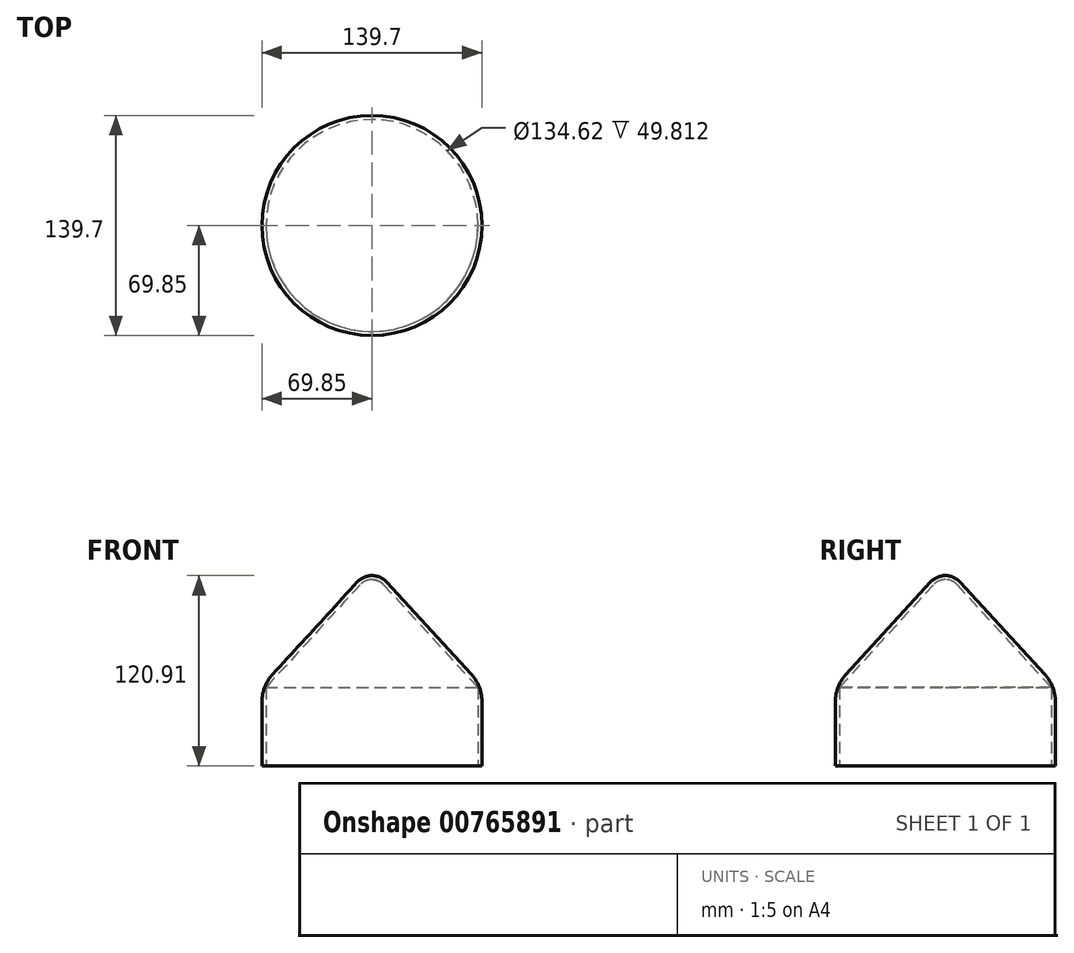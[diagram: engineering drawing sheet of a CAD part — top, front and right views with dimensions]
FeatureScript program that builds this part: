
annotation { "Feature Type Name" : "Feature", "Feature Type Description" : "" }
export const myFeature = defineFeature(function(context is Context, id is Id, definition is map)
    precondition{}
    {
        {
            var Q0;
            Q0=qCreatedBy(makeId("Front.planeOp"),FACE);
            var sketch = newSketch(context, id + "F0", { "sketchPlane" : qUnion([Q0])});
            skLineSegment(sketch, "E0", {"start": v(0, 0) * mm, "end": v(0, 76.2) * mm});
            skLineSegment(sketch, "E1", {"start": v(0, 76.2) * mm, "end": v(69.85, 0) * mm});
            skLineSegment(sketch, "E2", {"start": v(69.85, 0) * mm, "end": v(0, 0) * mm});
            skLineSegment(sketch, "E3", {"start": v(69.85, 0) * mm, "end": v(69.85, -50.8) * mm});
            skLineSegment(sketch, "E4", {"start": v(69.85, -50.8) * mm, "end": v(0, -50.8) * mm});
            skLineSegment(sketch, "E5", {"start": v(0, -50.8) * mm, "end": v(0, 0) * mm});
            skArc(sketch, "E6", {"start": v(9.36, 65.99) * mm, "mid": v(5.11, 69.03) * mm, "end": v(0, 70.1) * mm});
            skSolve(sketch);
        }
        {
            var Q0;
            Q0=makeQuery(id+"F0.imprint","IMPRINT",FACE,{"disambiguationData":[TD([[makeQuery(id+"F0.imprint","IMPRINT",EDGE,{"derivedFrom":sQuery(id+"F0.wireOp",EDGE,"E2")}),1.0]])]});
            var Q1;
            {var subQ0=sQuery(id+"F0.wireOp",EDGE,"E2");Q1=makeQuery(id+"F0.imprint","IMPRINT",FACE,{"disambiguationData":[TD([[makeQuery(id+"F0.imprint","IMPRINT",EDGE,{"derivedFrom":subQ0}),-1.0]])]});}
            var Q2;
            Q2=sQuery(id+"F0.wireOp",EDGE,"E0");
            revolve(context, id + "F1", {"surfaceOperationType" : NewSurfaceOperationType.NEW, "entities" : qUnion([Q0, Q1]), "axis" : qUnion([Q2]), "revolveType" : RevolveType.FULL});
        }
        {
            var Q0;
            Q0=makeQuery(id+"F1.opRevolve","SWEPT_FACE",FACE,{"disambiguationData":[OSD([sQuery(id+"F0.wireOp",EDGE,"E4")])]});
            shell(context, id + "F2", {"entities" : qUnion([Q0]), "thickness" : 2.54 * mm});
        }
        {
            var Q0;
            Q0=makeQuery(id+"F1.opRevolve","SWEPT_EDGE",EDGE,{"disambiguationData":[OSD([sQuery(id+"F0.wireOp",EDGE,"E1"),sQuery(id+"F0.wireOp",EDGE,"E2"),sQuery(id+"F0.wireOp",EDGE,"E3")])]});
            fillet(context, id + "F3", {"entities" : qUnion([Q0]), "radius" : 25.4 * mm, "tangentPropagation" : true, "allowEdgeOverflow" : false});
        }
    });
